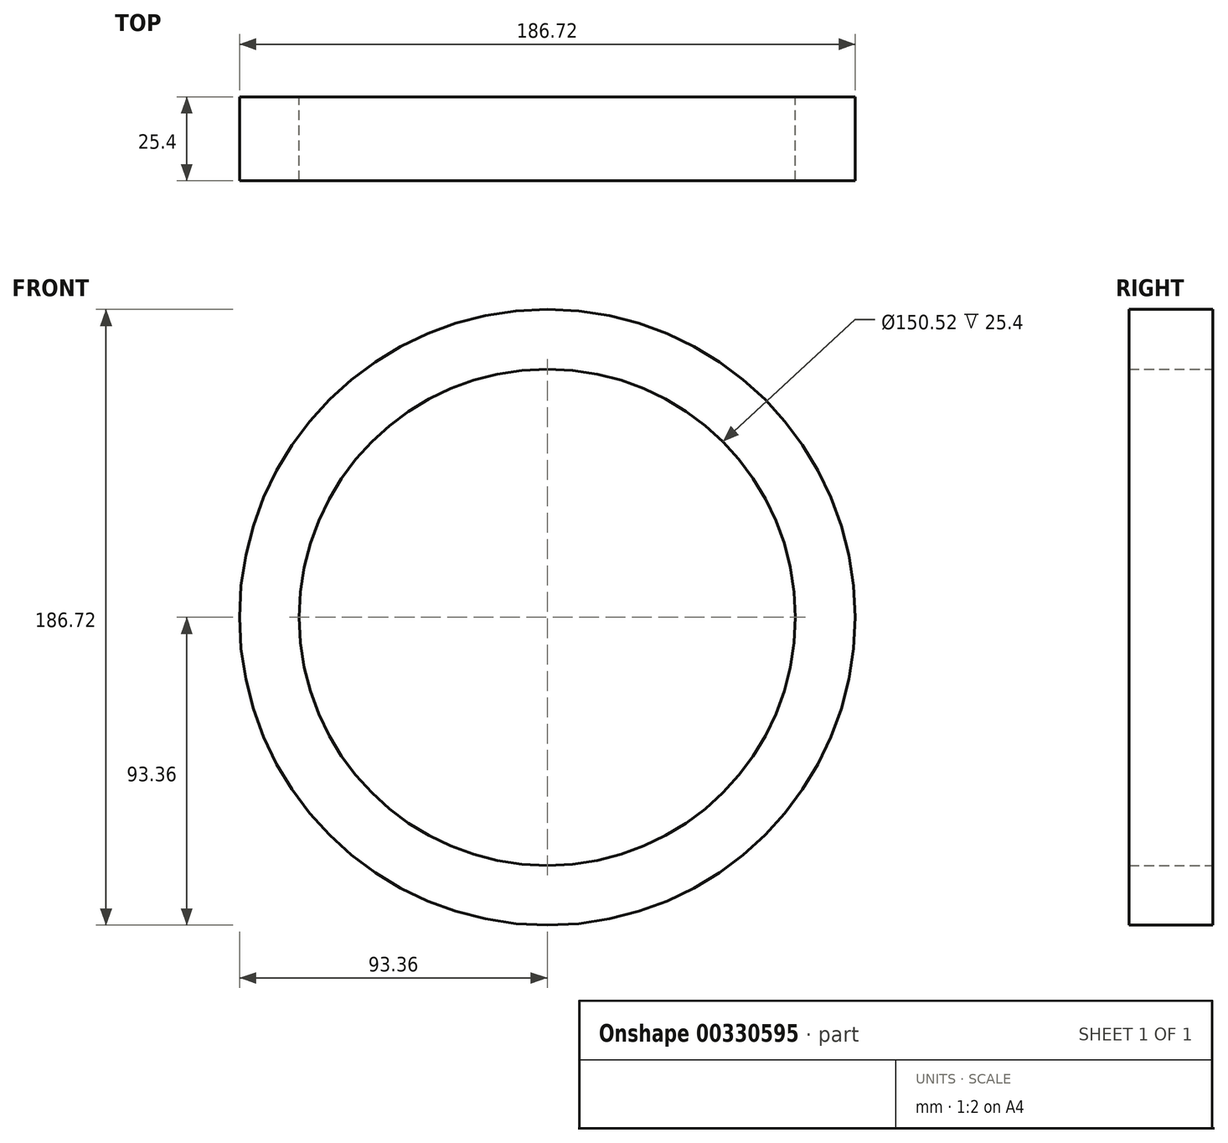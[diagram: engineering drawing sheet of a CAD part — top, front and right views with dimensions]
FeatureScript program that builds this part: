
annotation { "Feature Type Name" : "Feature", "Feature Type Description" : "" }
export const myFeature = defineFeature(function(context is Context, id is Id, definition is map)
    precondition{}
    {
        {
            var Q0;
            Q0=qCreatedBy(makeId("Front.planeOp"),FACE);
            var sketch = newSketch(context, id + "F0", { "sketchPlane" : qUnion([Q0])});
            skCircle(sketch, "E0", {"center": v(0, 0) * mm, "radius": 93.36 * mm});
            skCircle(sketch, "E1", {"center": v(0, 0) * mm, "radius": 75.26 * mm});
            skSolve(sketch);
        }
        {
            var Q0;
            Q0 = qSketchRegion(id + "F0", true);
            extrude(context, id + "F1", {"entities" : qUnion([Q0]), "endBound" : BoundingType.SYMMETRIC, "depth" : 25.4 * mm});
        }
    });
